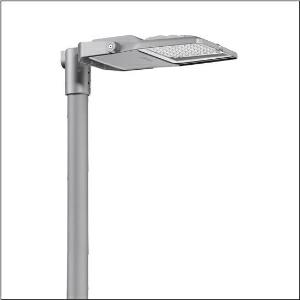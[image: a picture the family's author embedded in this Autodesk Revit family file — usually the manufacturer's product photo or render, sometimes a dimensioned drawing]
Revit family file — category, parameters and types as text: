
# Revit family: floodlight_fl_21_iq_mini___pl33t_5xa7772b2f3a_3cf2
name_source: partatom
category: Lighting Fixtures
units: mm (PartAtom-declared; Revit-internal decimal feet)

## family parameters
Cut with Voids When Loaded = No
Host = Face
Light Source = No
Part Type = Normal
Room Calculation Point = No
Round Connector Dimension = Use Diameter
Shared = No

## types (1)
- --- (1 x LED, 6170 lm, 45.5 W, 3000K)
    Apparent Load = 46 VA
    CIE Flux Codes = 26 75 99 100 100
    Color Rendering = 70
    Color Temperature = 3000K
    Default Elevation = 1800 mm
    Description = Floodlight FL 21 iQ mini, floodlight, primary light control with lens, of PMMA, primary optical cover: protective disc, of toughened safety glass, transparent, light distribution: PL33T, light emission: direct distribution, installation type: surface-mounted, LED, High Power LED, rated luminous flux: 6.170lm, luminous efficacy: 136lm/W, light colour: 730, colour temperature: 3000K, control: Auto-Match, Temp-Guard, Night-Set, Smart-Wire, Desk-Remote (wireless, voltage-free reading and setting of iQ features in the workshop via application-optimized NFC function/RFID function), optimised constant luminous flux control (CLO 2.0), Light-Fading, Lumen-Switch, with terminal, 6-pole, mains connection: 220..240V, AC, 50/60Hz, start of lifetime: 46W, end of service life: 48W, reduction: 22W, luminaire housing, of diecast aluminium, powder-coated, Siteco® metallic grey (DB 702S), corrosivity category C5 mid according to DIN EN ISO 12944, sealing non-destructively replaceable, please order mast flange separately, mast bracket, of steel, galvanised, powder-coated, protection rating (complete): IP66, insulation class (complete): insulation class II (safety insulation), certification: CE, ENEC, VDE, protection symbol: D, impact resistance: IK08, permissible operating ambient temperature: -40..+40°C, permissible operating ambient temperature for outdoor applications: -40..+50°C, standard: DIN EN 12944, LABS conformity tested according to VDMA 24364:2018-05, packaging unit: 1 piece

Light Distribution: PL33T
    Height = 70 mm
    Lamp = 1 x LED
    Lamp Light Flux = 6170 lm
    Lamp Power = 45.5 W
    Lamp count = 1
    Length = 485 mm
    Luminous efficacy = 136 lm/W
    Manufacturer = Siteco
    ModVariant = No
    Model = 5XA7772B2F3A
    Number of Poles = 1
    OnlyDefault = Yes
    Power Factor = 1
    Product Name = Floodlight FL 21 iQ mini | PL33T
    Product group = floodlight | pylon annexe
    ProductGroupID = 6200
    Protection Class = Protection class II
    Protection Degree = IP 66
    RLX_Detail_Level = 1
    RLX_Emergency_Light_Flux = 0 lm
    RLX_Emergency_Type = 0
    RLX_Emergency_Type_DB = No
    RlxData = <blob elided: 101101 chars, md5=f4e8925a>
    Socket = socket
    Standby Power = 0 W
    System Light Flux = 6170 lm
    System Power = 46 W
    Type Comments = factory setting: luminous flux: 100 % | dim-lin: 254 | 463 mA
    Type Image = l_1007125.jpg
    URL = http://relux.com
    VarID = @adj_100189
    Voltage = 0 V
    Weight = 0.00 kg
    Width = 337 mm

## geometry (parser evidence)
native form markers: Blend x4, Sweep x11
no freeform markers — native parametric forms only
